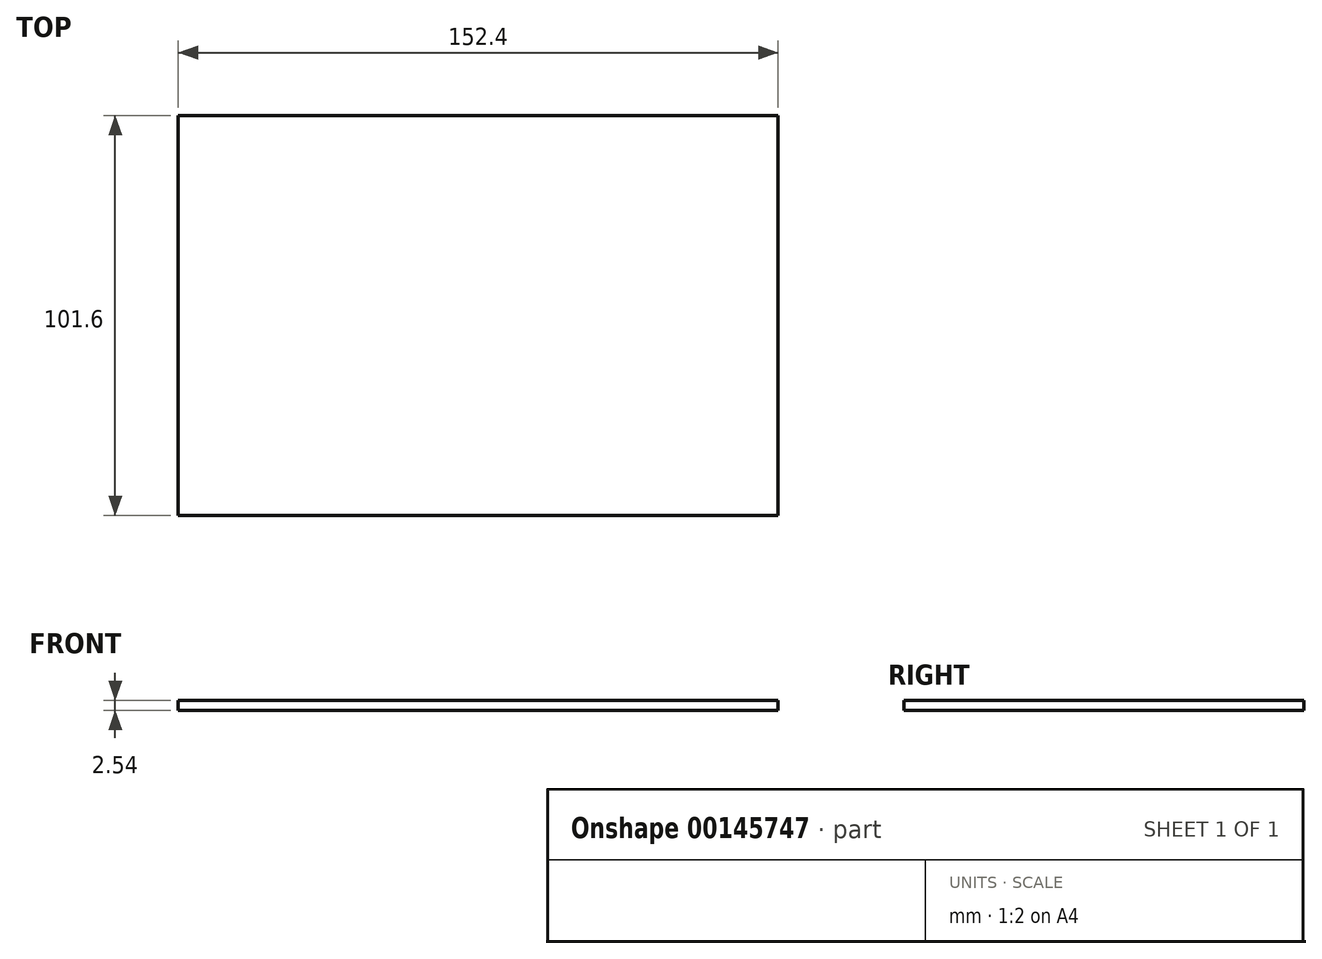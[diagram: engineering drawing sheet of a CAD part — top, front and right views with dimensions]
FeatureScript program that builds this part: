
annotation { "Feature Type Name" : "Feature", "Feature Type Description" : "" }
export const myFeature = defineFeature(function(context is Context, id is Id, definition is map)
    precondition{}
    {
        {
            var Q0;
            Q0=qCreatedBy(makeId("Front.planeOp"),FACE);
            var sketch = newSketch(context, id + "F0", { "sketchPlane" : qUnion([Q0])});
            skLineSegment(sketch, "E0.bottom", {"start": v(-56.8, -8.92) * mm, "end": v(95.6, -8.92) * mm});
            skLineSegment(sketch, "E0.top", {"start": v(-56.8, -11.46) * mm, "end": v(95.6, -11.46) * mm});
            skLineSegment(sketch, "E0.left", {"start": v(-56.8, -8.92) * mm, "end": v(-56.8, -11.46) * mm});
            skLineSegment(sketch, "E0.right", {"start": v(95.6, -8.92) * mm, "end": v(95.6, -11.46) * mm});
            skSolve(sketch);
        }
        {
            var Q0;
            Q0 = qSketchRegion(id + "F0", true);
            extrude(context, id + "F1", {"entities" : qUnion([Q0]), "depth" : 101.6 * mm});
        }
    });
